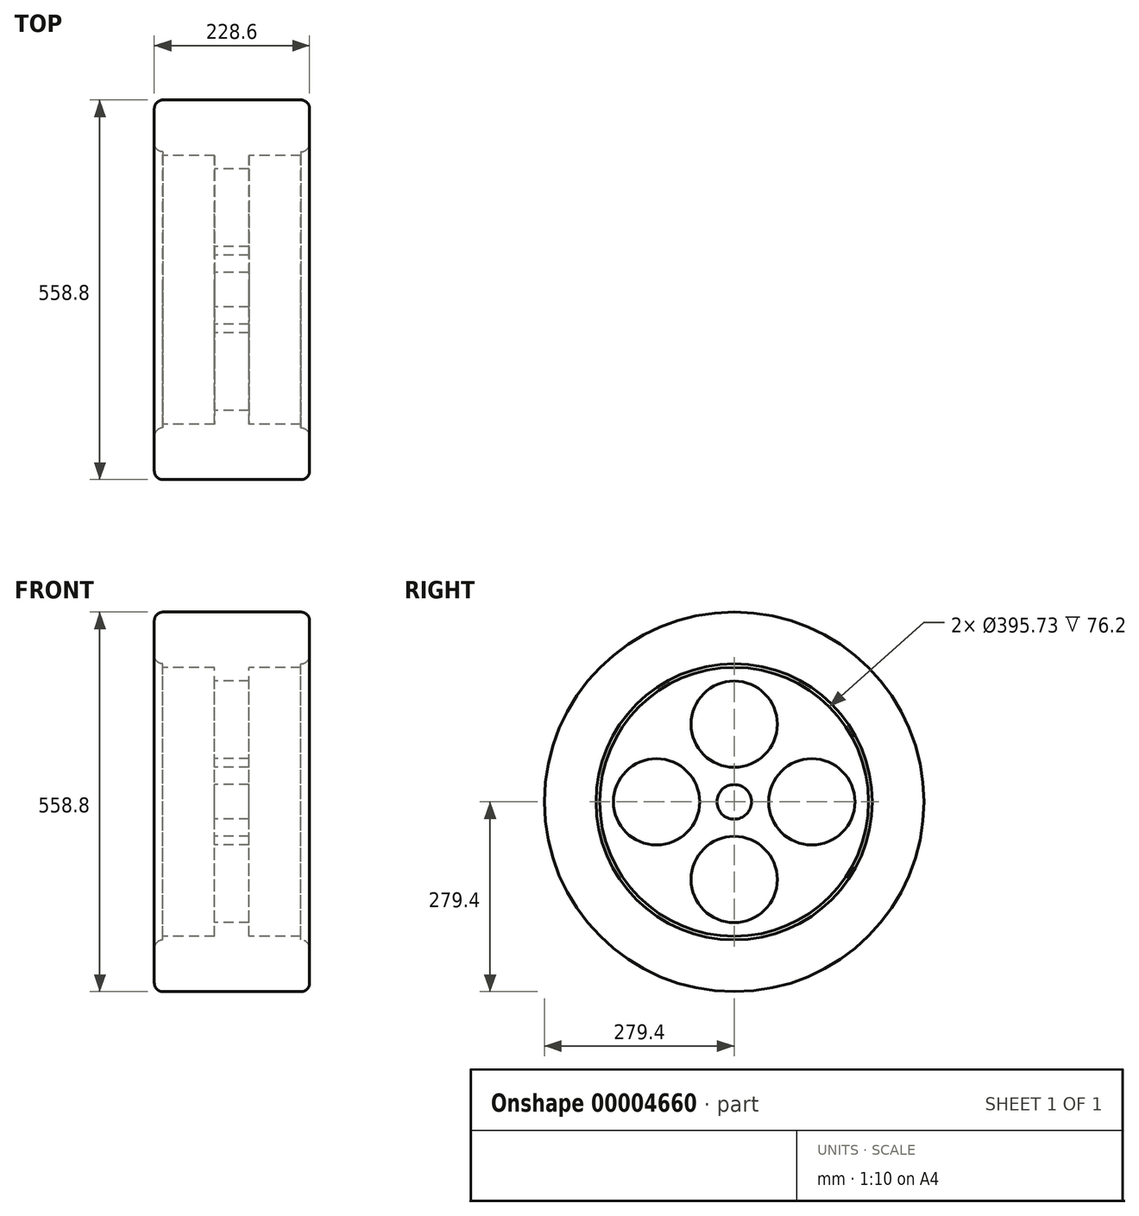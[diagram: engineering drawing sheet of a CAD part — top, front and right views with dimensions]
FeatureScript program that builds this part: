
annotation { "Feature Type Name" : "Feature", "Feature Type Description" : "" }
export const myFeature = defineFeature(function(context is Context, id is Id, definition is map)
    precondition{}
    {
        {
            var Q0;
            Q0=qCreatedBy(makeId("Front.planeOp"),FACE);
            var sketch = newSketch(context, id + "F0", { "sketchPlane" : qUnion([Q0])});
            skCircle(sketch, "E0", {"center": v(0, 0) * mm, "radius": 279.4 * mm});
            skCircle(sketch, "E1", {"center": v(0, 0) * mm, "radius": 203.2 * mm});
            skCircle(sketch, "E2", {"center": v(0, 0) * mm, "radius": 114.3 * mm, "construction": true});
            skLineSegment(sketch, "E3", {"start": v(0, 0) * mm, "end": v(-511.16, 0) * mm, "construction": true});
            skLineSegment(sketch, "E4", {"start": v(0, 0) * mm, "end": v(394.12, 0) * mm, "construction": true});
            skLineSegment(sketch, "E5", {"start": v(0, 0) * mm, "end": v(0, 354.47) * mm, "construction": true});
            skLineSegment(sketch, "E6", {"start": v(0, 0) * mm, "end": v(0, -279.4) * mm, "construction": true});
            skCircle(sketch, "E7", {"center": v(-114.3, 0) * mm, "radius": 63.5 * mm});
            skCircle(sketch, "E8", {"center": v(114.3, 0) * mm, "radius": 63.5 * mm});
            skCircle(sketch, "E9", {"center": v(0, -114.3) * mm, "radius": 63.5 * mm});
            skCircle(sketch, "E10", {"center": v(0, 114.3) * mm, "radius": 63.5 * mm});
            skCircle(sketch, "E11", {"center": v(0, 0) * mm, "radius": 25.4 * mm});
            skCircle(sketch, "E12", {"center": v(0, 0) * mm, "radius": 197.87 * mm});
            skSolve(sketch);
        }
        {
            var Q0;
            Q0=makeQuery(id+"F0.imprint","IMPRINT",FACE,{"disambiguationData":[TD([[makeQuery(id+"F0.imprint","IMPRINT",EDGE,{"derivedFrom":sQuery(id+"F0.wireOp",EDGE,"E7")}),-1.0]])]});
            extrude(context, id + "F1", {"entities" : qUnion([Q0]), "endBound" : BoundingType.SYMMETRIC, "depth" : 50.8 * mm});
        }
        {
            var Q0;
            Q0=makeQuery(id+"F0.imprint","IMPRINT",FACE,{"disambiguationData":[TD([[makeQuery(id+"F0.imprint","IMPRINT",EDGE,{"derivedFrom":sQuery(id+"F0.wireOp",EDGE,"E0")}),1.0]])]});
            extrude(context, id + "F2", {"entities" : qUnion([Q0]), "endBound" : BoundingType.SYMMETRIC, "depth" : 228.6 * mm});
        }
        {
            var Q0;
            Q0=makeQuery(id+"F2.opExtrude","CAP_EDGE",EDGE,{"disambiguationData":[OSD([sQuery(id+"F0.wireOp",EDGE,"E0")])],"isStart":false});
            var Q1;
            Q1=makeQuery(id+"F2.opExtrude","CAP_EDGE",EDGE,{"disambiguationData":[OSD([sQuery(id+"F0.wireOp",EDGE,"E1")])],"isStart":false});
            fillet(context, id + "F3", {"entities" : qUnion([Q0, Q1]), "radius" : 12.7 * mm, "tangentPropagation" : true, "allowEdgeOverflow" : false});
        }
        {
            var Q0;
            Q0=makeQuery(id+"F2.opExtrude","CAP_EDGE",EDGE,{"disambiguationData":[OSD([sQuery(id+"F0.wireOp",EDGE,"E0")])],"isStart":true});
            var Q1;
            Q1=makeQuery(id+"F2.opExtrude","CAP_EDGE",EDGE,{"disambiguationData":[OSD([sQuery(id+"F0.wireOp",EDGE,"E1")])],"isStart":true});
            fillet(context, id + "F4", {"entities" : qUnion([Q0, Q1]), "radius" : 12.7 * mm, "tangentPropagation" : true, "allowEdgeOverflow" : false});
        }
        {
            var Q0;
            Q0=makeQuery(id+"F0.imprint","IMPRINT",FACE,{"disambiguationData":[TD([[makeQuery(id+"F0.imprint","IMPRINT",EDGE,{"derivedFrom":sQuery(id+"F0.wireOp",EDGE,"E12")}),-1.0]])]});
            extrude(context, id + "F5", {"entities" : qUnion([Q0]), "operationType" : NewBodyOperationType.ADD, "endBound" : BoundingType.SYMMETRIC, "depth" : 203.2 * mm});
        }
        {
            var Q0;
            Q0=makeQuery(id+"F1.opExtrude","SWEPT_BODY",BODY,{"disambiguationData":[OSD([sQuery(id+"F0.wireOp",EDGE,"E7"),sQuery(id+"F0.wireOp",EDGE,"E8"),sQuery(id+"F0.wireOp",EDGE,"E9"),sQuery(id+"F0.wireOp",EDGE,"E10"),sQuery(id+"F0.wireOp",EDGE,"E11"),sQuery(id+"F0.wireOp",EDGE,"E12")])]});
            var Q1;
            Q1=sQuery(id+"F0.wireOp",EDGE,"E5");
            transform(context, id + "F6", {"entities" : qUnion([Q0]), "transformType" : TransformType.ROTATION, "transformAxis" : qUnion([Q1]), "angle" : 90 * degree, "makeCopy" : false});
        }
    });
